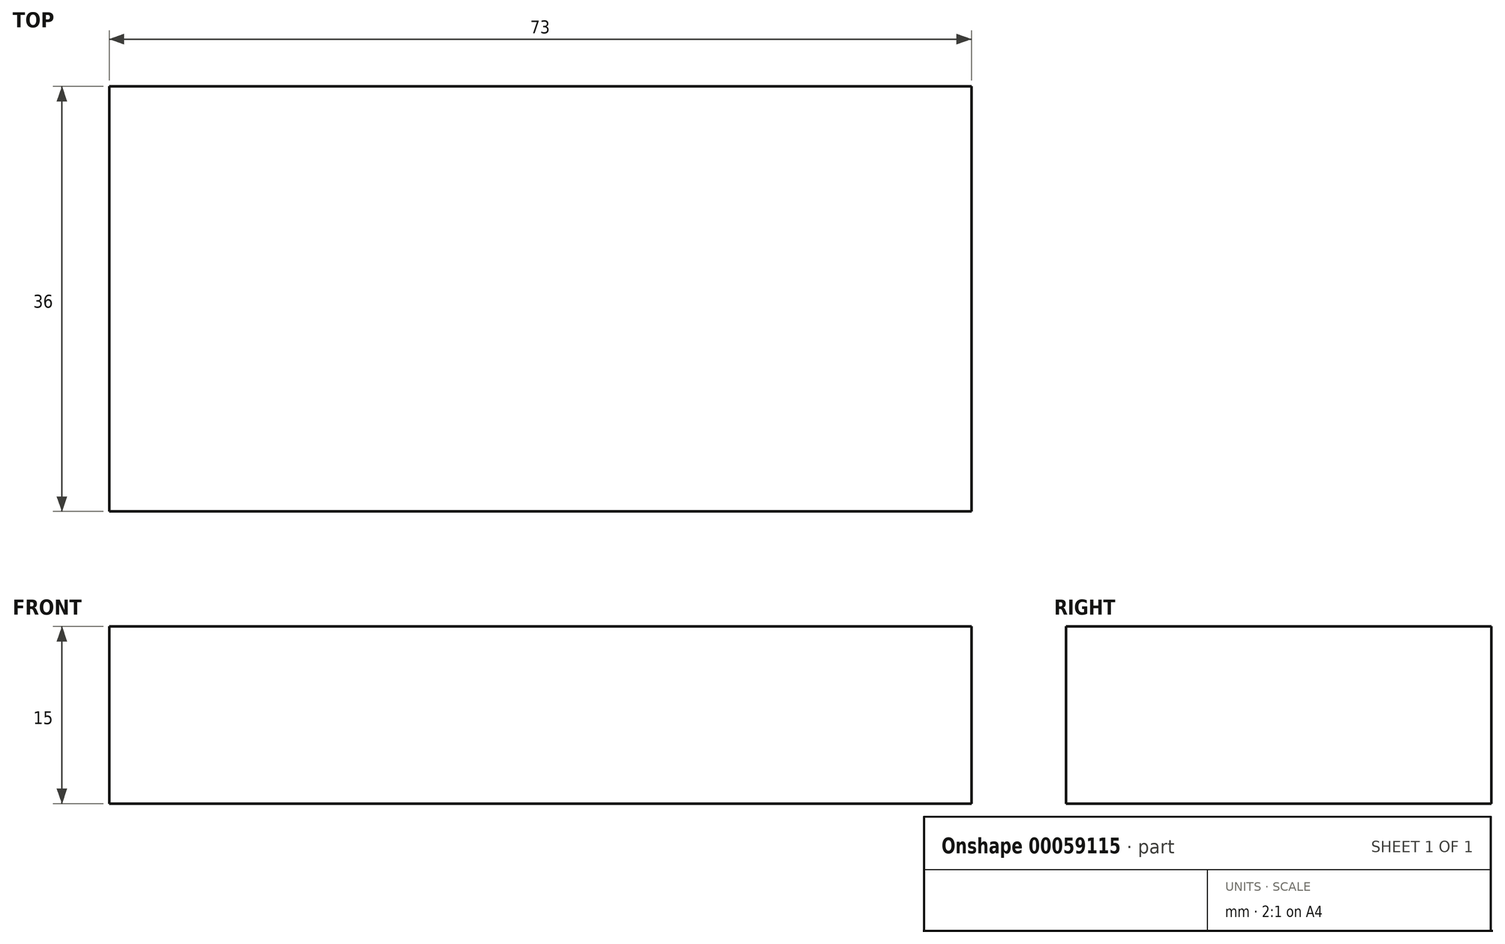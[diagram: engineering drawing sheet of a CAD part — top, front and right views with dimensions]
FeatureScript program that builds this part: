
annotation { "Feature Type Name" : "Feature", "Feature Type Description" : "" }
export const myFeature = defineFeature(function(context is Context, id is Id, definition is map)
    precondition{}
    {
        {
            var Q0;
            Q0=qCreatedBy(makeId("Top.planeOp"),FACE);
            var sketch = newSketch(context, id + "F0", { "sketchPlane" : qUnion([Q0])});
            skLineSegment(sketch, "E0.rect.bottom", {"start": v(36.5, 18) * mm, "end": v(-36.5, 18) * mm});
            skLineSegment(sketch, "E0.rect.top", {"start": v(36.5, -18) * mm, "end": v(-36.5, -18) * mm});
            skLineSegment(sketch, "E0.rect.left", {"start": v(36.5, 18) * mm, "end": v(36.5, -18) * mm});
            skLineSegment(sketch, "E0.rect.right", {"start": v(-36.5, 18) * mm, "end": v(-36.5, -18) * mm});
            skPoint(sketch, "E0.rect.middle", {"position": v(0, 0) * mm});
            skSolve(sketch);
        }
        {
            var Q0;
            Q0 = qSketchRegion(id + "F0", true);
            extrude(context, id + "F1", {"entities" : qUnion([Q0]), "depth" : 15 * mm});
        }
    });
